# Revit family: e8eed37b-caac-41ba-9030-df46564a57da
name_source: partatom
category: Doors
revit_build: Autodesk Revit 2014 (Build: 20130308_1515(x64)
units: mm (PartAtom-declared; Revit-internal decimal feet)

## types (2) — shared parameters
Analytic Construction = <None>
Assembly Code = B2030400
Description = Wayne Dalton Between Jamb Mounted Shutter Door - Security 523 as Specified
Fire Rating = as Specified
Frame Offset Extrusions = Yes
Function = Interior
Height = 0' - 0"
Hood Above Opening = 0' - 0"
Jamb Above Opening = 0' - 0"
Jamb Depth = 0' - 1 1/4"
Jamb Width = 0' - 3 7/8"
Keynote = 08 33 23
Manufacturer = Wayne Dalton
Manufacturer Website = http://www.wayne-dalton.com
Max Height = 14' - 0"
Max Width = 20' - 0"
Model = Security 523 Between Jamb
Product Data = http://www.arcat.com
Rough Height = 0' - 0"
Rough Width = 0' - 0"
Sales Information = http://www.wayne-dalton.com
Standards Conformance = as Specified
Thickness = 0' - 0"
URL = http://www.wayne-dalton.com
Wall Closure = By host
Width = 0' - 0"
hoodextra = No
zero-valued in all types: Expected Lifespan (Years), Maintenance Schedule (Months), Warranty Duration (Years)

## per-type parameters (varying)
| type | Bottom Bar A | Bottom Bar B |
| Cylinder Bottom Bar | No | Yes |
| Compact Bottom Bar | Yes | No |

## geometry (parser evidence)
native form markers: Extrusion x1, Sweep x3
no freeform markers — native parametric forms only
